# Revit family: 02-68-030-DN50-300
name_source: partatom
category: Pipe Accessories
units: mm (PartAtom-declared; Revit-internal decimal feet)

## family parameters
Always vertical = No
Cut with Voids When Loaded = No
OmniClass Number = 23.60.00.00
OmniClass Title = General Purpose: Services
Part Type = Valve - Breaks Into
Round Connector Dimension = Use Diameter
Shared = Yes
Work Plane-Based = No

## types (9) — shared parameters
Body_Wallthickness = 15 mm  [stored 0.0492126 ft]
DN 050 = Yes
DN050_PN25 = 02-050-68-07605
DN065_PN25 = 02-065-68-07605
DN080_PN25 = 02-080-68-07605
DN100_PN25 = 02-100-68-07605
DN125_PN25 = 02-125-68-07605
DN150_PN25 = 02-150-68-07605
DN200_PN25 = 02-200-68-07605
DN250_PN25 = 02-250-68-07605
DN300_PN25 = 02-300-68-07605
Ftc = 4 mm  [stored 0.0131234 ft]
Gearbox_Flangethickness = 10 mm  [stored 0.0328084 ft]
Name_Height_reference = 10 mm  [stored 0.0328084 ft]
Rib_Height_Reference_3 = 100 mm
Rib_Thickness = 18 mm  [stored 0.0590551 ft]
Search_table = 02-68-030-DN50-300
Tf = 26 mm
URL product pages = https://www.avkvalves.com
zero-valued in all types: Bottom_Reference

## per-type parameters (varying)
- DN 050: At=60.5 mm; Body_Height=110 mm; Body_depth=121 mm; Body_width=74 mm; Bonnet_Flange_Depth=118 mm; Bonnet_Flange_Width=90 mm; Bonnet_Flange_cut=7.5 mm  [stored 0.0246063 ft]; Bonnet_Flange_thickness=15 mm  [stored 0.0492126 ft]; Bonnet_Height=41.25 mm; Bonnet_Reference_height=100 mm; Bonnet_Thickness=75.48 mm; Bt=75.48 mm; Bt_2=68 mm; CL=92 mm; CL _Thickness=15 mm  [stored 0.0492126 ft]; CL_2=62 mm; CL_Thickness 2=20 mm  [stored 0.0656168 ft]; Cut_Reference=500 mm; DN 065=No; DN 080=No; DN 100=No; DN 125=No; DN 150=No; DN 200=No; DN 250=No; DN 300=No; Description_=AVK_GATE_VALVE,FLANGED; F=7 mm  [stored 0.0229659 ft]; F1=8.5 mm; F2=29 mm  [stored 0.0951444 ft]; Fillet_Thickness=6 mm  [stored 0.019685 ft]; Flange_OR=82.5 mm; Flange_Thickness=19 mm  [stored 0.062336 ft]; Flange_Thickness_cut=28.75 mm; Ftc_reference_height=82.5 mm; Gearbox_Flange_Dia=15 mm  [stored 0.0492126 ft]; H=241 mm; H3=324 mm; Horizontal_Flange_width=166 mm; ID (Radius)=25 mm  [stored 0.082021 ft]; L=250 mm; L_Dia=50 mm; Name_Reference=90 mm; Name_Width=37 mm; Nominal Diameter (DN)=50 mm; R1tv=825 mm; R2f=15 mm  [stored 0.0492126 ft]; RF_Dia=50 mm; Rf=276.67 mm; Rib_Height_Reference_1=120 mm; Rib_Height_Reference_2=110 mm; Rib_Height_Reference_4=60 mm; Rib_Width_1=37 mm; Rib_Width_2=37 mm; Rib_Width_3=37 mm; Rib_depth_1=37 mm; Rib_depth_2=37 mm; Rib_depth_3=37 mm; Rt=275 mm
- DN 065: At=54.5 mm; Body_Height=125 mm; Body_depth=109 mm; Body_width=74 mm; Bonnet_Flange_Depth=135 mm; Bonnet_Flange_Width=85 mm; Bonnet_Flange_cut=7.5 mm  [stored 0.0246063 ft]; Bonnet_Flange_thickness=15 mm  [stored 0.0492126 ft]; Bonnet_Height=46.25 mm; Bonnet_Reference_height=115 mm; Bonnet_Thickness=75.48 mm; Bt=75.48 mm; Bt_2=68 mm; CL=102 mm; CL _Thickness=14.17 mm; CL_2=72 mm; CL_Thickness 2=18.33 mm; Cut_Reference=542 mm; DN 065=Yes; DN 080=Yes; DN 100=Yes; DN 125=Yes; DN 150=Yes; DN 200=Yes; DN 250=Yes; DN 300=Yes; Description_=AVK_GATE-VALVE,FLANGED; F=8.5 mm; F1=10 mm  [stored 0.0328084 ft]; F2=34 mm  [stored 0.111549 ft]; Fillet_Thickness=6 mm  [stored 0.019685 ft]; Flange_OR=92.5 mm; Flange_Thickness=19 mm  [stored 0.062336 ft]; Flange_Thickness_cut=30 mm  [stored 0.0984252 ft]; Ftc_reference_height=92.5 mm; Gearbox_Flange_Dia=14.17 mm; H=271 mm; H3=364 mm; Horizontal_Flange_width=186 mm; ID (Radius)=32.5 mm  [stored 0.106627 ft]; L=271 mm; L_Dia=65 mm; Name_Reference=100 mm; Name_Width=37 mm; Nominal Diameter (DN)=65 mm; R1tv=925 mm; R2f=15 mm  [stored 0.0492126 ft]; RF_Dia=59 mm; Rf=310 mm; Rib_Height_Reference_1=120 mm; Rib_Height_Reference_2=110 mm; Rib_Height_Reference_4=75 mm; Rib_Width_1=37 mm; Rib_Width_2=37 mm; Rib_Width_3=37 mm; Rib_depth_1=37 mm; Rib_depth_2=37 mm; Rib_depth_3=37 mm; Rt=308.33 mm
- DN 080: At=62 mm; Body_Height=155 mm; Body_depth=124 mm; Body_width=79 mm; Bonnet_Flange_Depth=150 mm; Bonnet_Flange_Width=100 mm; Bonnet_Flange_cut=7.5 mm  [stored 0.0246063 ft]; Bonnet_Flange_thickness=15 mm  [stored 0.0492126 ft]; Bonnet_Height=50 mm; Bonnet_Reference_height=145 mm; Bonnet_Thickness=80.58 mm; Bt=80.58 mm; Bt_2=73 mm; CL=98 mm; CL _Thickness=16.67 mm; CL_2=68 mm; CL_Thickness 2=23.33 mm; Cut_Reference=560 mm; DN 065=Yes; DN 080=Yes; DN 100=Yes; DN 125=Yes; DN 150=Yes; DN 200=Yes; DN 250=Yes; DN 300=Yes; Description_=AVK_GATE_VALVE,FLANGED; F=8.5 mm; F1=10 mm  [stored 0.0328084 ft]; F2=34 mm  [stored 0.111549 ft]; Fillet_Thickness=6 mm  [stored 0.019685 ft]; Flange_OR=100 mm; Flange_Thickness=19 mm  [stored 0.062336 ft]; Flange_Thickness_cut=30 mm  [stored 0.0984252 ft]; Ftc_reference_height=100 mm; Gearbox_Flange_Dia=16.67 mm; H=297 mm; H3=397 mm; Horizontal_Flange_width=200 mm; ID (Radius)=40 mm; L=280 mm; L_Dia=80 mm; Name_Reference=130 mm; Name_Width=39.5 mm; Nominal Diameter (DN)=80 mm; R1tv=1000 mm; R2f=15 mm  [stored 0.0492126 ft]; RF_Dia=66 mm; Rf=333.33 mm; Rib_Height_Reference_1=120 mm; Rib_Height_Reference_2=110 mm; Rib_Height_Reference_4=85 mm; Rib_Width_1=39.5 mm; Rib_Width_2=39.5 mm; Rib_Width_3=39.5 mm; Rib_depth_1=39.5 mm; Rib_depth_2=39.5 mm; Rib_depth_3=39.5 mm; Rt=333.33 mm
- DN 100: At=77 mm; Body_Height=175 mm; Body_depth=154 mm; Body_width=95 mm; Bonnet_Flange_Depth=180 mm; Bonnet_Flange_Width=122 mm; Bonnet_Flange_cut=7.5 mm  [stored 0.0246063 ft]; Bonnet_Flange_thickness=15 mm  [stored 0.0492126 ft]; Bonnet_Height=58.75 mm; Bonnet_Reference_height=165 mm; Bonnet_Thickness=96.9 mm; Bt=96.9 mm; Bt_2=89 mm; CL=111 mm; CL _Thickness=20.33 mm; CL_2=81 mm; CL_Thickness 2=30.67 mm; Cut_Reference=600 mm; DN 065=Yes; DN 080=Yes; DN 100=Yes; DN 125=Yes; DN 150=Yes; DN 200=Yes; DN 250=Yes; DN 300=Yes; Description_=AVK_GATE_VALVE,FLANGED; F=9.5 mm  [stored 0.031168 ft]; F1=11 mm  [stored 0.0360892 ft]; F2=38 mm; Fillet_Thickness=6 mm  [stored 0.019685 ft]; Flange_OR=117.5 mm; Flange_Thickness=19 mm  [stored 0.062336 ft]; Flange_Thickness_cut=33.75 mm  [stored 0.110728 ft]; Ftc_reference_height=117.5 mm; Gearbox_Flange_Dia=20.33 mm; H=334 mm; H3=444 mm; Horizontal_Flange_width=220 mm; ID (Radius)=50 mm; L=300 mm; L_Dia=100 mm; Name_Reference=150 mm; Name_Width=47.5 mm; Nominal Diameter (DN)=100 mm; R1tv=1175 mm; R2f=15 mm  [stored 0.0492126 ft]; RF_Dia=78 mm; Rf=366.67 mm; Rib_Height_Reference_1=120 mm; Rib_Height_Reference_2=110 mm; Rib_Height_Reference_4=90 mm; Rib_Width_1=47.5 mm; Rib_Width_2=47.5 mm; Rib_Width_3=47.5 mm; Rib_depth_1=47.5 mm; Rib_depth_2=47.5 mm; Rib_depth_3=47.5 mm; Rt=391.67 mm
- DN 150: At=113 mm; Body_Height=210 mm; Body_depth=226 mm; Body_width=138 mm; Bonnet_Flange_Depth=250 mm; Bonnet_Flange_Width=144 mm; Bonnet_Flange_cut=7.5 mm  [stored 0.0246063 ft]; Bonnet_Flange_thickness=15 mm  [stored 0.0492126 ft]; Bonnet_Height=75 mm; Bonnet_Reference_height=200 mm; Bonnet_Thickness=140.76 mm; Bt=140.76 mm; Bt_2=132 mm; CL=190 mm; CL _Thickness=24 mm  [stored 0.0787402 ft]; CL_2=160 mm; CL_Thickness 2=38 mm; Cut_Reference=700 mm; DN 065=Yes; DN 080=Yes; DN 100=Yes; DN 125=Yes; DN 150=Yes; DN 200=Yes; DN 250=Yes; DN 300=Yes; Description_=AVK_GATE_VALVE,FLANGED; F=9.5 mm  [stored 0.031168 ft]; F1=11 mm  [stored 0.0360892 ft]; F2=38 mm; Fillet_Thickness=12 mm  [stored 0.0393701 ft]; Flange_OR=150 mm; Flange_Thickness=19 mm  [stored 0.062336 ft]; Flange_Thickness_cut=37.5 mm; Ftc_reference_height=150 mm; Gearbox_Flange_Dia=24 mm  [stored 0.0787402 ft]; H=448 mm; H3=598 mm; Horizontal_Flange_width=300 mm; ID (Radius)=75 mm; L=350 mm; L_Dia=150 mm; Name_Reference=170 mm; Name_Width=69 mm; Nominal Diameter (DN)=150 mm; R1tv=1500 mm; R2f=30 mm  [stored 0.0984252 ft]; RF_Dia=106 mm; Rf=500 mm; Rib_Height_Reference_1=120 mm; Rib_Height_Reference_2=110 mm; Rib_Height_Reference_4=150 mm; Rib_Width_1=69 mm; Rib_Width_2=69 mm; Rib_Width_3=69 mm; Rib_depth_1=69 mm; Rib_depth_2=69 mm; Rib_depth_3=69 mm; Rt=500 mm
- DN 200: At=128.5 mm; Body_Height=289 mm; Body_depth=257 mm; Body_width=160 mm; Bonnet_Flange_Depth=283 mm; Bonnet_Flange_Width=163 mm; Bonnet_Flange_cut=12.5 mm  [stored 0.0410105 ft]; Bonnet_Flange_thickness=25 mm  [stored 0.082021 ft]; Bonnet_Height=90 mm; Bonnet_Reference_height=279 mm; Bonnet_Thickness=163.2 mm; Bt=163.2 mm; Bt_2=154 mm; CL=221 mm; CL _Thickness=27.17 mm; CL_2=191 mm; CL_Thickness 2=44.33 mm; Cut_Reference=800 mm; DN 065=Yes; DN 080=Yes; DN 100=Yes; DN 125=Yes; DN 150=Yes; DN 200=Yes; DN 250=Yes; DN 300=Yes; Description_=AVK_GATE_VALVE,FLANGED; F=12 mm  [stored 0.0393701 ft]; F1=14 mm  [stored 0.0459318 ft]; F2=42 mm; Fillet_Thickness=24 mm  [stored 0.0787402 ft]; Flange_OR=180 mm; Flange_Thickness=20 mm  [stored 0.0656168 ft]; Flange_Thickness_cut=40 mm; Ftc_reference_height=180 mm; Gearbox_Flange_Dia=27.17 mm; H=562 mm; H3=742 mm; Horizontal_Flange_width=360 mm; ID (Radius)=100 mm; L=400 mm; L_Dia=200 mm; Name_Reference=200 mm; Name_Width=80 mm; Nominal Diameter (DN)=200 mm; R1tv=1800 mm; R2f=60 mm; RF_Dia=133 mm; Rf=600 mm; Rib_Height_Reference_1=120 mm; Rib_Height_Reference_2=110 mm; Rib_Height_Reference_4=180 mm; Rib_Width_1=80 mm; Rib_Width_2=80 mm; Rib_Width_3=80 mm; Rib_depth_1=80 mm; Rib_depth_2=80 mm; Rib_depth_3=80 mm; Rt=600 mm
- DN 250: At=167 mm; Body_Height=350 mm; Body_depth=334 mm; Body_width=162 mm; Bonnet_Flange_Depth=372 mm; Bonnet_Flange_Width=162 mm; Bonnet_Flange_cut=12.5 mm  [stored 0.0410105 ft]; Bonnet_Flange_thickness=25 mm  [stored 0.082021 ft]; Bonnet_Height=106.25 mm; Bonnet_Reference_height=340 mm; Bonnet_Thickness=165.24 mm; Bt=165.24 mm; Bt_2=156 mm; CL=257 mm; CL _Thickness=27 mm  [stored 0.0885827 ft]; CL_2=227 mm; CL_Thickness 2=44 mm; Cut_Reference=900 mm; DN 065=Yes; DN 080=Yes; DN 100=Yes; DN 125=Yes; DN 150=Yes; DN 200=Yes; DN 250=Yes; DN 300=Yes; Description_=AVK_GATE_VALVE,FLANGED; F=13.5 mm  [stored 0.0442913 ft]; F1=15.5 mm  [stored 0.050853 ft]; F2=47 mm; Fillet_Thickness=24 mm  [stored 0.0787402 ft]; Flange_OR=212.5 mm; Flange_Thickness=22 mm  [stored 0.0721785 ft]; Flange_Thickness_cut=43.75 mm; Ftc_reference_height=212.5 mm; Gearbox_Flange_Dia=27 mm  [stored 0.0885827 ft]; H=664 mm; H3=877 mm; Horizontal_Flange_width=426 mm; ID (Radius)=125 mm; L=450 mm; L_Dia=250 mm; Name_Reference=200 mm; Name_Width=81 mm; Nominal Diameter (DN)=250 mm; R1tv=2125 mm; R2f=60 mm; RF_Dia=160 mm; Rf=710 mm; Rib_Height_Reference_1=90 mm; Rib_Height_Reference_2=110 mm; Rib_Height_Reference_4=250 mm; Rib_Width_1=190 mm; Rib_Width_2=81 mm; Rib_Width_3=81 mm; Rib_depth_1=358 mm; Rib_depth_2=81 mm; Rib_depth_3=81 mm; Rt=708.33 mm
- DN 300: At=215 mm; Body_Height=415 mm; Body_depth=430 mm; Body_width=160 mm; Bonnet_Flange_Depth=448 mm; Bonnet_Flange_Width=196 mm; Bonnet_Flange_cut=17.5 mm  [stored 0.0574147 ft]; Bonnet_Flange_thickness=35 mm  [stored 0.114829 ft]; Bonnet_Height=121.25 mm; Bonnet_Reference_height=405 mm; Bonnet_Thickness=163.2 mm; Bt=163.2 mm; Bt_2=154 mm; CL=268 mm; CL _Thickness=32.67 mm; CL_2=238 mm; CL_Thickness 2=55.33 mm; Cut_Reference=1000 mm; DN 065=Yes; DN 080=Yes; DN 100=Yes; DN 125=Yes; DN 150=Yes; DN 200=Yes; DN 250=Yes; DN 300=Yes; Description_=AVK_GATE_VALVE,FLANGED; F=13.5 mm  [stored 0.0442913 ft]; F1=15.5 mm  [stored 0.050853 ft]; F2=47 mm; Fillet_Thickness=24 mm  [stored 0.0787402 ft]; Flange_OR=242.5 mm; Flange_Thickness=24.5 mm  [stored 0.0803806 ft]; Flange_Thickness_cut=46.25 mm; Ftc_reference_height=242.5 mm; Gearbox_Flange_Dia=32.67 mm; H=740 mm; H3=968 mm; Horizontal_Flange_width=456 mm; ID (Radius)=150 mm; L=500 mm; L_Dia=300 mm; Name_Reference=300 mm; Name_Width=80 mm; Nominal Diameter (DN)=300 mm; R1tv=2425 mm; R2f=60 mm; RF_Dia=185 mm; Rf=760 mm; Rib_Height_Reference_1=113 mm; Rib_Height_Reference_2=285 mm; Rib_Height_Reference_4=325 mm; Rib_Width_1=196 mm; Rib_Width_2=196 mm; Rib_Width_3=80 mm; Rib_depth_1=438 mm; Rib_depth_2=438 mm; Rib_depth_3=80 mm; Rt=808.33 mm
- DN 125: At=109 mm; Body_Height=170 mm; Body_depth=218 mm; Body_width=112 mm; Bonnet_Flange_Depth=235 mm; Bonnet_Flange_Width=120 mm; Bonnet_Flange_cut=7.5 mm  [stored 0.0246063 ft]; Bonnet_Flange_thickness=15 mm  [stored 0.0492126 ft]; Bonnet_Height=67.5 mm; Bonnet_Reference_height=160 mm; Bonnet_Thickness=114.24 mm; Bt=114.24 mm; Bt_2=106 mm; CL=158 mm; CL _Thickness=20 mm  [stored 0.0656168 ft]; CL_2=128 mm; CL_Thickness 2=30 mm  [stored 0.0984252 ft]; Cut_Reference=650 mm; DN 065=Yes; DN 080=Yes; DN 100=Yes; DN 125=Yes; DN 150=Yes; DN 200=Yes; DN 250=Yes; DN 300=Yes; Description_=AVK_GATE_VALVE,FLANGED; F=9.5 mm  [stored 0.031168 ft]; F1=11 mm  [stored 0.0360892 ft]; F2=38 mm; Fillet_Thickness=6 mm  [stored 0.019685 ft]; Flange_OR=135 mm; Flange_Thickness=19 mm  [stored 0.062336 ft]; Flange_Thickness_cut=36.25 mm; Ftc_reference_height=135 mm; Gearbox_Flange_Dia=20 mm  [stored 0.0656168 ft]; H=376 mm; H3=501 mm; Horizontal_Flange_width=250 mm; ID (Radius)=62.5 mm; L=325 mm; L_Dia=125 mm; Name_Reference=165 mm; Name_Width=56 mm; Nominal Diameter (DN)=125 mm; R1tv=1350 mm; R2f=15 mm  [stored 0.0492126 ft]; RF_Dia=92 mm; Rf=416.67 mm; Rib_Height_Reference_1=120 mm; Rib_Height_Reference_2=110 mm; Rib_Height_Reference_4=120 mm; Rib_Width_1=56 mm; Rib_Width_2=56 mm; Rib_Width_3=56 mm; Rib_depth_1=56 mm; Rib_depth_2=56 mm; Rib_depth_3=56 mm; Rt=450 mm

note: [stored X ft] marks values corroborated as IEEE doubles in the binary element streams (Revit-internal decimal feet)

## geometry (parser evidence)
native form markers: Sweep x4
no freeform markers — native parametric forms only
